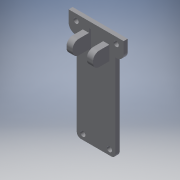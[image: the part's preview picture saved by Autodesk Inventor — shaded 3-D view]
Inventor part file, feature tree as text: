
AUTODESK INVENTOR PART (.ipt)
format: ipt  version: 2016 (Build 200138000, 138)  size: 199,168 bytes
history: native  units: mm
features: extrude x5, sketch x5, fillet x1
ambient origin geometry x8: Origin, YZ Plane, XZ Plane, XY Plane, X Axis, Y Axis, Z Axis, Center Point
bodies: Solid1 (feature_tree)
feature tree (11):
  extrude  "Extrusion1"  Depth=2.0mm TaperAngle=0.0deg
  extrude  "Extrusion2"  Depth=3.0mm
  fillet  "Fillet1"  Radius=7.0mm
  extrude  "Extrusion4"  Depth=3.0mm
  extrude  "Extrusion5"  Depth=5.0mm
  extrude  "Extrusion6"  Depth=2.0mm
  sketch  "Sketch1"  dims[d6=3.5mm d7=1.0mm d8=1.0mm d9=3.5mm d10=0.0mm d11=2.5mm d12=1.0mm d13=2.0mm d14=0.0mm]
  sketch  "Sketch2"  dims[d15=7.0mm d18=3.0mm d21=7.0mm]
  sketch  "Sketch4"  dims[d22=8.0mm d23=0.0mm d24=3.0mm]
  sketch  "Sketch5"  dims[d32=3.0mm d36=5.0mm]
  sketch  "Sketch6"  dims[d37=2.0mm d38=2.0mm d39=1.0mm d40=0.0mm d41=3.0mm d42=3.0mm d43=4.5mm d44=3.5mm d45=3.5mm d46=15.0mm d47=0.0mm d48=3.0mm d49=5.0mm d50=3.0mm d51=0.0mm]
